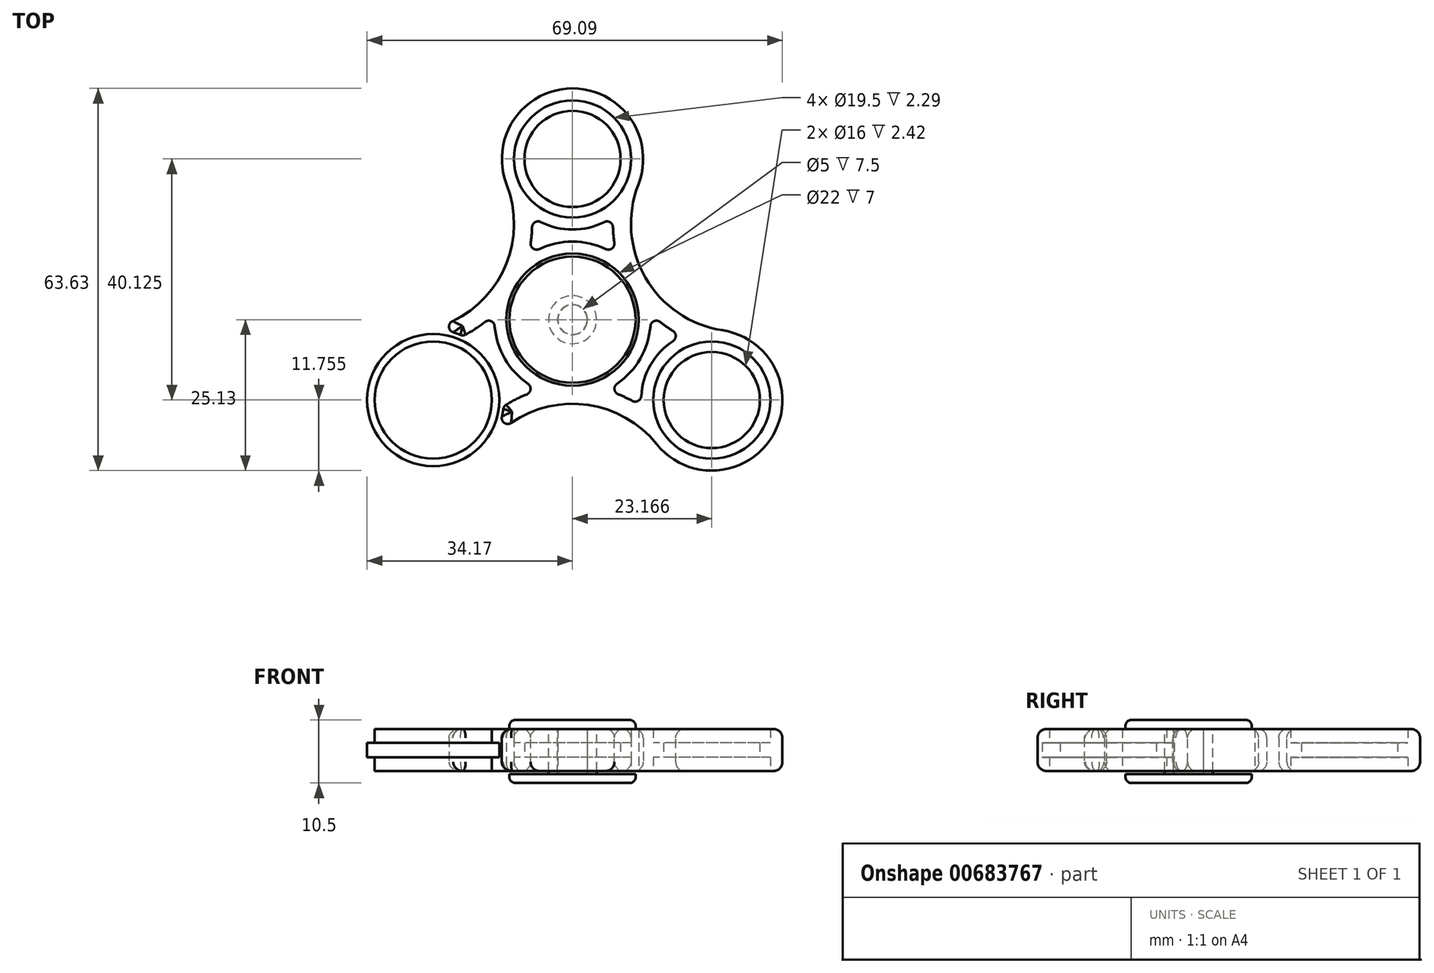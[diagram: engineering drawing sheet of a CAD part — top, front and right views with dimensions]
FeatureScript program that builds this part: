
annotation { "Feature Type Name" : "Feature", "Feature Type Description" : "" }
export const myFeature = defineFeature(function(context is Context, id is Id, definition is map)
    precondition{}
    {
        {
            assignVariable(context, id + "F0", {"name" : "bearing_thickness", "anyValue" : 7});
        }
        {
            assignVariable(context, id + "F1", {"name" : "coin_thickness", "anyValue" : 1.79});
        }
        {
            var Q0;
            Q0=qCreatedBy(makeId("Top.planeOp"),FACE);
            var sketch = newSketch(context, id + "F2", { "sketchPlane" : qUnion([Q0])});
            skCircle(sketch, "E0", {"center": v(0, 0) * mm, "radius": 11 * mm});
            skCircle(sketch, "E1", {"center": v(0, 0) * mm, "radius": 13 * mm});
            skCircle(sketch, "E2", {"center": v(0, 26.75) * mm, "radius": 9.75 * mm});
            skCircle(sketch, "E3", {"center": v(0, 26.75) * mm, "radius": 11.75 * mm});
            skLineSegment(sketch, "E4", {"start": v(0, 0) * mm, "end": v(23.17, -13.37) * mm, "construction": true});
            skLineSegment(sketch, "E5", {"start": v(0, 0) * mm, "end": v(0, 26.75) * mm, "construction": true});
            skCircle(sketch, "E6", {"center": v(23.17, -13.38) * mm, "radius": 9.75 * mm});
            skCircle(sketch, "E7", {"center": v(23.17, -13.38) * mm, "radius": 11.75 * mm});
            skCircle(sketch, "E8.MirrorC", {"center": v(-23.17, -13.38) * mm, "radius": 11.75 * mm});
            skCircle(sketch, "E9.MirrorC", {"center": v(-23.17, -13.38) * mm, "radius": 9.75 * mm});
            skLineSegment(sketch, "E10", {"start": v(-23.17, -13.38) * mm, "end": v(0, 26.75) * mm, "construction": true});
            skLineSegment(sketch, "E11", {"start": v(0, 26.75) * mm, "end": v(23.17, -13.38) * mm, "construction": true});
            skLineSegment(sketch, "E12", {"start": v(-23.17, -13.38) * mm, "end": v(23.17, -13.38) * mm, "construction": true});
            skLineSegment(sketch, "E13", {"start": v(6.18, 52.15) * mm, "end": v(-41.18, -29.88) * mm, "construction": true});
            skArc(sketch, "E14", {"start": v(-24.94, -1.76) * mm, "mid": v(-12.12, 7) * mm, "end": v(-10.95, 22.48) * mm});
            skArc(sketch, "E15.1.0", {"start": v(14, -20.72) * mm, "mid": v(0, -14) * mm, "end": v(-14, -20.72) * mm});
            skArc(sketch, "E15.2.0", {"start": v(10.95, 22.48) * mm, "mid": v(12.12, 7) * mm, "end": v(24.94, -1.76) * mm});
            skArc(sketch, "E16", {"start": v(-11.46, -14.42) * mm, "mid": v(-8.61, -12.85) * mm, "end": v(-5.56, -11.75) * mm});
            skArc(sketch, "E17", {"start": v(5.56, -11.75) * mm, "mid": v(8.61, -12.85) * mm, "end": v(11.46, -14.42) * mm});
            skArc(sketch, "E18", {"start": v(18.22, -2.72) * mm, "mid": v(15.44, -1.03) * mm, "end": v(12.96, 1.06) * mm});
            skArc(sketch, "E19", {"start": v(7.4, 10.69) * mm, "mid": v(6.83, 13.89) * mm, "end": v(6.75, 17.14) * mm});
            skArc(sketch, "E20", {"start": v(-18.22, -2.72) * mm, "mid": v(-15.44, -1.03) * mm, "end": v(-12.96, 1.06) * mm});
            skArc(sketch, "E21", {"start": v(-6.75, 17.14) * mm, "mid": v(-6.83, 13.89) * mm, "end": v(-7.4, 10.69) * mm});
            skLineSegment(sketch, "E22", {"start": v(-27.65, 15.97) * mm, "end": v(0, 0) * mm, "construction": true});
            skLineSegment(sketch, "E23", {"start": v(0, 0) * mm, "end": v(27.65, 15.97) * mm, "construction": true});
            skLineSegment(sketch, "E24", {"start": v(0, 0) * mm, "end": v(0, -31.93) * mm, "construction": true});
            skSolve(sketch);
        }
        {
            var Q0;
            Q0=makeQuery(id+"F2.imprint","IMPRINT",FACE,{"disambiguationData":[TD([[makeQuery(id+"F2.imprint","IMPRINT",EDGE,{"derivedFrom":sQuery(id+"F2.wireOp",EDGE,"E2")}),-1.0]])]});
            var Q1;
            {var subQ0=sQuery(id+"F2.wireOp",EDGE,"E14");Q1=makeQuery(id+"F2.imprint","IMPRINT",FACE,{"disambiguationData":[TD([[makeQuery(id+"F2.imprint","IMPRINT",EDGE,{"derivedFrom":subQ0}),-1.0]])]});}
            var Q2;
            {var subQ0=sQuery(id+"F2.wireOp",EDGE,"E15.2.0");Q2=makeQuery(id+"F2.imprint","IMPRINT",FACE,{"disambiguationData":[TD([[makeQuery(id+"F2.imprint","IMPRINT",EDGE,{"derivedFrom":subQ0}),-1.0]])]});}
            var Q3;
            Q3=makeQuery(id+"F2.imprint","IMPRINT",FACE,{"disambiguationData":[TD([[makeQuery(id+"F2.imprint","IMPRINT",EDGE,{"derivedFrom":sQuery(id+"F2.wireOp",EDGE,"E6")}),-1.0]])]});
            var Q4;
            {var subQ0=sQuery(id+"F2.wireOp",EDGE,"E15.1.0");Q4=makeQuery(id+"F2.imprint","IMPRINT",FACE,{"disambiguationData":[TD([[makeQuery(id+"F2.imprint","IMPRINT",EDGE,{"derivedFrom":subQ0}),-1.0]])]});}
            var Q5;
            Q5=makeQuery(id+"F2.imprint","IMPRINT",FACE,{"disambiguationData":[TD([[makeQuery(id+"F2.imprint","IMPRINT",EDGE,{"derivedFrom":sQuery(id+"F2.wireOp",EDGE,"E9.MirrorC")}),1.0]])]});
            var Q6;
            Q6=makeQuery(id+"F2.imprint","IMPRINT",FACE,{"disambiguationData":[TD([[makeQuery(id+"F2.imprint","IMPRINT",EDGE,{"derivedFrom":sQuery(id+"F2.wireOp",EDGE,"E0")}),-1.0]])]});
            extrude(context, id + "F3", {"entities" : qUnion([Q0, Q1, Q2, Q3, Q4, Q5, Q6]), "depth" : (getVariable(context, 'bearing_thickness')) * mm, "offsetDistance" : 25 * mm});
        }
        {
            var Q0;
            Q0=makeQuery(id+"F3.opExtrude","SWEPT_EDGE",EDGE,{"disambiguationData":[OSD([sQuery(id+"F2.wireOp",EDGE,"E3"),sQuery(id+"F2.wireOp",EDGE,"8bf2e3d8-5615-4718-9600-4cf8535fb07a.trimOffspring")])]});
            var Q1;
            Q1=makeQuery(id+"F3.opExtrude","SWEPT_EDGE",EDGE,{"disambiguationData":[OSD([sQuery(id+"F2.wireOp",EDGE,"E3"),sQuery(id+"F2.wireOp",EDGE,"a5741abb-2599-4cf7-b8e6-df64fac0e9c5.trimOffspring")])]});
            var Q2;
            Q2=makeQuery(id+"F3.opExtrude","SWEPT_EDGE",EDGE,{"disambiguationData":[OSD([sQuery(id+"F2.wireOp",EDGE,"E1"),sQuery(id+"F2.wireOp",EDGE,"8bf2e3d8-5615-4718-9600-4cf8535fb07a.trimOffspring")])]});
            var Q3;
            Q3=makeQuery(id+"F3.opExtrude","SWEPT_EDGE",EDGE,{"disambiguationData":[OSD([sQuery(id+"F2.wireOp",EDGE,"E1"),sQuery(id+"F2.wireOp",EDGE,"a5741abb-2599-4cf7-b8e6-df64fac0e9c5.trimOffspring")])]});
            var Q4;
            Q4=makeQuery(id+"F3.opExtrude","SWEPT_EDGE",EDGE,{"disambiguationData":[OSD([sQuery(id+"F2.wireOp",EDGE,"E7"),sQuery(id+"F2.wireOp",EDGE,"336d5f12-412a-4e1d-b3b8-37471ca9ab7e.trimOffspring")])]});
            var Q5;
            Q5=makeQuery(id+"F3.opExtrude","SWEPT_EDGE",EDGE,{"disambiguationData":[OSD([sQuery(id+"F2.wireOp",EDGE,"E1"),sQuery(id+"F2.wireOp",EDGE,"336d5f12-412a-4e1d-b3b8-37471ca9ab7e.trimOffspring")])]});
            var Q6;
            Q6=makeQuery(id+"F3.opExtrude","SWEPT_EDGE",EDGE,{"disambiguationData":[OSD([sQuery(id+"F2.wireOp",EDGE,"E1"),sQuery(id+"F2.wireOp",EDGE,"f4dcb5e2-fab5-4d8d-8cc3-e8628036cf0f.trimOffspring")])]});
            var Q7;
            Q7=makeQuery(id+"F3.opExtrude","SWEPT_EDGE",EDGE,{"disambiguationData":[OSD([sQuery(id+"F2.wireOp",EDGE,"E7"),sQuery(id+"F2.wireOp",EDGE,"f4dcb5e2-fab5-4d8d-8cc3-e8628036cf0f.trimOffspring")])]});
            var Q8;
            Q8=makeQuery(id+"F3.opExtrude","SWEPT_EDGE",EDGE,{"disambiguationData":[OSD([sQuery(id+"F2.wireOp",EDGE,"E1"),sQuery(id+"F2.wireOp",EDGE,"8b9473ec-3ca8-44b6-a831-62ebe32cb006.trimOffspring")])]});
            var Q9;
            Q9=makeQuery(id+"F3.opExtrude","SWEPT_EDGE",EDGE,{"disambiguationData":[OSD([sQuery(id+"F2.wireOp",EDGE,"E8.MirrorC"),sQuery(id+"F2.wireOp",EDGE,"8b9473ec-3ca8-44b6-a831-62ebe32cb006.trimOffspring")])]});
            var Q10;
            Q10=makeQuery(id+"F3.opExtrude","SWEPT_EDGE",EDGE,{"disambiguationData":[OSD([sQuery(id+"F2.wireOp",EDGE,"E8.MirrorC"),sQuery(id+"F2.wireOp",EDGE,"a5d12814-47ba-4dec-aad6-e72ed20c2dc8.trimOffspring")])]});
            var Q11;
            Q11=makeQuery(id+"F3.opExtrude","SWEPT_EDGE",EDGE,{"disambiguationData":[OSD([sQuery(id+"F2.wireOp",EDGE,"E1"),sQuery(id+"F2.wireOp",EDGE,"a5d12814-47ba-4dec-aad6-e72ed20c2dc8.trimOffspring")])]});
            fillet(context, id + "F4", {"entities" : qUnion([Q0, Q1, Q2, Q3, Q4, Q5, Q6, Q7, Q8, Q9, Q10, Q11]), "radius" : 1 * mm, "tangentPropagation" : true, "allowEdgeOverflow" : false});
        }
        {
            var Q0;
            Q0=makeQuery(id+"F3.opExtrude","CAP_EDGE",EDGE,{"disambiguationData":[OSD([sQuery(id+"F2.wireOp",EDGE,"E14")])],"isStart":false});
            var Q1;
            {var subQ0=sQuery(id+"F2.wireOp",EDGE,"E3");Q1=makeQuery(id+"F3.opExtrude","CAP_EDGE",EDGE,{"disambiguationData":[OSD([subQ0]),TDD([makeQuery(id+"F2.imprint","IMPRINT",EDGE,{"disambiguationData":[TD([[makeQuery(id+"F2.imprint","INTERSECT",VERTEX,{"derivedFrom":[subQ0,sQuery(id+"F2.wireOp",EDGE,"a5741abb-2599-4cf7-b8e6-df64fac0e9c5.trimOffspring")]}),1.0]])],"derivedFrom":subQ0})])],"isStart":false});}
            var Q2;
            {var subQ0=sQuery(id+"F2.wireOp",EDGE,"E1");Q2=makeQuery(id+"F3.opExtrude","CAP_EDGE",EDGE,{"disambiguationData":[OSD([subQ0]),TDD([makeQuery(id+"F2.imprint","IMPRINT",EDGE,{"disambiguationData":[TD([[makeQuery(id+"F2.imprint","INTERSECT",VERTEX,{"derivedFrom":[subQ0,sQuery(id+"F2.wireOp",EDGE,"f4dcb5e2-fab5-4d8d-8cc3-e8628036cf0f.trimOffspring")]}),-1.0]])],"derivedFrom":subQ0})])],"isStart":false});}
            var Q3;
            {var subQ0=sQuery(id+"F2.wireOp",EDGE,"E8.MirrorC");Q3=makeQuery(id+"F3.opExtrude","CAP_EDGE",EDGE,{"disambiguationData":[OSD([subQ0]),TDD([makeQuery(id+"F2.imprint","IMPRINT",EDGE,{"disambiguationData":[TD([[makeQuery(id+"F2.imprint","INTERSECT",VERTEX,{"derivedFrom":[subQ0,sQuery(id+"F2.wireOp",EDGE,"a5d12814-47ba-4dec-aad6-e72ed20c2dc8.trimOffspring")]}),1.0]])],"derivedFrom":subQ0})])],"isStart":false});}
            var Q4;
            Q4=makeQuery(id+"F3.opExtrude","CAP_EDGE",EDGE,{"disambiguationData":[OSD([sQuery(id+"F2.wireOp",EDGE,"E15.1.0")])],"isStart":true});
            var Q5;
            {var subQ0=sQuery(id+"F2.wireOp",EDGE,"E8.MirrorC");Q5=makeQuery(id+"F3.opExtrude","CAP_EDGE",EDGE,{"disambiguationData":[OSD([subQ0]),TDD([makeQuery(id+"F2.imprint","IMPRINT",EDGE,{"disambiguationData":[TD([[makeQuery(id+"F2.imprint","INTERSECT",VERTEX,{"derivedFrom":[subQ0,sQuery(id+"F2.wireOp",EDGE,"a5d12814-47ba-4dec-aad6-e72ed20c2dc8.trimOffspring")]}),1.0]])],"derivedFrom":subQ0})])],"isStart":true});}
            var Q6;
            {var subQ0=sQuery(id+"F2.wireOp",EDGE,"E7");Q6=makeQuery(id+"F3.opExtrude","CAP_EDGE",EDGE,{"disambiguationData":[OSD([subQ0]),TDD([makeQuery(id+"F2.imprint","IMPRINT",EDGE,{"disambiguationData":[TD([[makeQuery(id+"F2.imprint","INTERSECT",VERTEX,{"derivedFrom":[subQ0,sQuery(id+"F2.wireOp",EDGE,"f4dcb5e2-fab5-4d8d-8cc3-e8628036cf0f.trimOffspring")]}),1.0]])],"derivedFrom":subQ0})])],"isStart":true});}
            var Q7;
            {var subQ0=sQuery(id+"F2.wireOp",EDGE,"E1");Q7=makeQuery(id+"F3.opExtrude","CAP_EDGE",EDGE,{"disambiguationData":[OSD([subQ0]),TDD([makeQuery(id+"F2.imprint","IMPRINT",EDGE,{"disambiguationData":[TD([[makeQuery(id+"F2.imprint","INTERSECT",VERTEX,{"derivedFrom":[subQ0,sQuery(id+"F2.wireOp",EDGE,"a5741abb-2599-4cf7-b8e6-df64fac0e9c5.trimOffspring")]}),-1.0]])],"derivedFrom":subQ0})])],"isStart":true});}
            fillet(context, id + "F5", {"entities" : qUnion([Q0, Q1, Q2, Q3, Q4, Q5, Q6, Q7]), "radius" : 1.5 * mm, "tangentPropagation" : true, "allowEdgeOverflow" : false});
        }
        {
            var Q0;
            Q0=qCreatedBy(makeId("Top.planeOp"),FACE);
            cPlane(context, id + "F6", {"entities" : qUnion([Q0]), "cplaneType" : CPlaneType.OFFSET, "offset" : (getVariable(context, 'bearing_thickness') / 2) * mm, "width" : 150 * mm, "height" : 150 * mm});
        }
        {
            var Q0;
            Q0=qCreatedBy(id+"F6.planeOp",FACE);
            var sketch = newSketch(context, id + "F7", { "sketchPlane" : qUnion([Q0])});
            skCircle(sketch, "E25", {"center": v(0, 26.75) * mm, "radius": 11 * mm});
            skCircle(sketch, "E26", {"center": v(0, 26.75) * mm, "radius": 8 * mm});
            skCircle(sketch, "E27.1.0", {"center": v(-23.17, -13.37) * mm, "radius": 11 * mm});
            skCircle(sketch, "E27.1.1", {"center": v(-23.17, -13.37) * mm, "radius": 8 * mm});
            skCircle(sketch, "E27.2.0", {"center": v(23.17, -13.37) * mm, "radius": 11 * mm});
            skCircle(sketch, "E27.2.1", {"center": v(23.17, -13.37) * mm, "radius": 8 * mm});
            skPoint(sketch, "E27.center", {"position": v(0, 0) * mm});
            skSolve(sketch);
        }
        {
            var Q0;
            Q0=makeQuery(id+"F7.imprint","IMPRINT",FACE,{"disambiguationData":[TD([[makeQuery(id+"F7.imprint","IMPRINT",EDGE,{"derivedFrom":sQuery(id+"F7.wireOp",EDGE,"E25")}),1.0]])]});
            var Q1;
            Q1=makeQuery(id+"F7.imprint","IMPRINT",FACE,{"disambiguationData":[TD([[makeQuery(id+"F7.imprint","IMPRINT",EDGE,{"derivedFrom":sQuery(id+"F7.wireOp",EDGE,"E27.1.0")}),1.0]])]});
            var Q2;
            Q2=makeQuery(id+"F7.imprint","IMPRINT",FACE,{"disambiguationData":[TD([[makeQuery(id+"F7.imprint","IMPRINT",EDGE,{"derivedFrom":sQuery(id+"F7.wireOp",EDGE,"E27.2.0")}),1.0]])]});
            extrude(context, id + "F8", {"entities" : qUnion([Q0, Q1, Q2]), "operationType" : NewBodyOperationType.ADD, "endBound" : BoundingType.SYMMETRIC, "depth" : (getVariable(context, 'bearing_thickness') - 2 * getVariable(context, 'coin_thickness') - 1) * mm, "offsetDistance" : 25 * mm});
        }
        {
            var Q0;
            Q0=makeQuery(id+"F5.opFillet","SPLIT",FACE,{"disambiguationData":[OD(3.0)],"derivedFrom":makeQuery(id+"F3.opExtrude","CAP_FACE",FACE,{"disambiguationData":[OSD([sQuery(id+"F2.wireOp",EDGE,"E0"),sQuery(id+"F2.wireOp",EDGE,"E1"),sQuery(id+"F2.wireOp",EDGE,"E2"),sQuery(id+"F2.wireOp",EDGE,"E3"),sQuery(id+"F2.wireOp",EDGE,"E6"),sQuery(id+"F2.wireOp",EDGE,"E7"),sQuery(id+"F2.wireOp",EDGE,"E8.MirrorC"),sQuery(id+"F2.wireOp",EDGE,"E9.MirrorC"),sQuery(id+"F2.wireOp",EDGE,"E14"),sQuery(id+"F2.wireOp",EDGE,"E15.1.0"),sQuery(id+"F2.wireOp",EDGE,"E15.2.0"),sQuery(id+"F2.wireOp",EDGE,"E16"),sQuery(id+"F2.wireOp",EDGE,"E17"),sQuery(id+"F2.wireOp",EDGE,"E18"),sQuery(id+"F2.wireOp",EDGE,"E19"),sQuery(id+"F2.wireOp",EDGE,"E20"),sQuery(id+"F2.wireOp",EDGE,"E21")])],"isStart":false})});
            var sketch = newSketch(context, id + "F9", { "sketchPlane" : qUnion([Q0])});
            skCircle(sketch, "E28", {"center": v(0, 0) * mm, "radius": 10.5 * mm});
            skSolve(sketch);
        }
        {
            var Q0;
            Q0=makeQuery(id+"F9.imprint","IMPRINT",FACE,{"disambiguationData":[TD([[makeQuery(id+"F9.imprint","IMPRINT",EDGE,{"derivedFrom":sQuery(id+"F9.wireOp",EDGE,"E28")}),1.0]])]});
            extrude(context, id + "F10", {"entities" : qUnion([Q0]), "depth" : 1.5 * mm, "offsetDistance" : 25 * mm});
        }
        {
            var Q0;
            Q0=makeQuery(id+"F10.opExtrude","CAP_FACE",FACE,{"disambiguationData":[OSD([sQuery(id+"F9.wireOp",EDGE,"E28")])],"isStart":true});
            var sketch = newSketch(context, id + "F11", { "sketchPlane" : qUnion([Q0])});
            skCircle(sketch, "E29", {"center": v(0, 0) * mm, "radius": 4 * mm});
            skCircle(sketch, "E30", {"center": v(0, 0) * mm, "radius": 2.5 * mm});
            skSolve(sketch);
        }
        {
            var Q0;
            Q0=makeQuery(id+"F11.imprint","IMPRINT",FACE,{"disambiguationData":[TD([[makeQuery(id+"F11.imprint","IMPRINT",EDGE,{"derivedFrom":sQuery(id+"F11.wireOp",EDGE,"E29")}),1.0]])]});
            extrude(context, id + "F12", {"entities" : qUnion([Q0]), "operationType" : NewBodyOperationType.ADD, "depth" : (getVariable(context, 'bearing_thickness') + 0.5) * mm, "offsetDistance" : 25 * mm});
        }
        {
            var Q0;
            Q0=makeQuery(id+"F12.opExtrude","CAP_FACE",FACE,{"disambiguationData":[OSD([sQuery(id+"F11.wireOp",EDGE,"E29"),sQuery(id+"F11.wireOp",EDGE,"E30")])],"isStart":false});
            var sketch = newSketch(context, id + "F13", { "sketchPlane" : qUnion([Q0])});
            skCircle(sketch, "E31", {"center": v(0, 0) * mm, "radius": 10.5 * mm});
            skSolve(sketch);
        }
        {
            var Q0;
            Q0=makeQuery(id+"F13.imprint","IMPRINT",FACE,{"disambiguationData":[TD([[makeQuery(id+"F13.imprint","IMPRINT",EDGE,{"derivedFrom":sQuery(id+"F13.wireOp",EDGE,"E31")}),1.0]])]});
            var Q1;
            Q1=makeQuery(id+"F13.imprint","IMPRINT",FACE,{"disambiguationData":[TD([[makeQuery(id+"F13.imprint","IMPRINT",EDGE,{"derivedFrom":makeQuery(id+"F12.opExtrude","CAP_EDGE",EDGE,{"disambiguationData":[OSD([sQuery(id+"F11.wireOp",EDGE,"E29")])],"isStart":false})}),1.0]])]});
            var Q2;
            Q2=makeQuery(id+"F13.imprint","IMPRINT",FACE,{"disambiguationData":[TD([[makeQuery(id+"F13.imprint","IMPRINT",EDGE,{"derivedFrom":makeQuery(id+"F12.opExtrude","CAP_EDGE",EDGE,{"disambiguationData":[OSD([sQuery(id+"F11.wireOp",EDGE,"E30")])],"isStart":false})}),1.0]])]});
            extrude(context, id + "F14", {"entities" : qUnion([Q0, Q1, Q2]), "depth" : 1.5 * mm, "offsetDistance" : 25 * mm});
        }
        {
            var Q0;
            Q0=makeQuery(id+"F10.opExtrude","CAP_EDGE",EDGE,{"disambiguationData":[OSD([sQuery(id+"F9.wireOp",EDGE,"E28")])],"isStart":false});
            var Q1;
            Q1=makeQuery(id+"F14.opExtrude","CAP_EDGE",EDGE,{"disambiguationData":[OSD([sQuery(id+"F13.wireOp",EDGE,"E31")])],"isStart":false});
            fillet(context, id + "F15", {"entities" : qUnion([Q0, Q1]), "radius" : 1 * mm, "tangentPropagation" : true, "allowEdgeOverflow" : false});
        }
        {
            var Q0;
            Q0=makeQuery(id+"F14.opExtrude","CAP_FACE",FACE,{"disambiguationData":[OSD([sQuery(id+"F13.wireOp",EDGE,"E31")])],"isStart":true});
            var sketch = newSketch(context, id + "F16", { "sketchPlane" : qUnion([Q0])});
            skCircle(sketch, "E32", {"center": v(0, 0) * mm, "radius": 2.45 * mm});
            skSolve(sketch);
        }
        {
            var Q0;
            Q0=makeQuery(id+"F16.imprint","IMPRINT",FACE,{"disambiguationData":[TD([[makeQuery(id+"F16.imprint","IMPRINT",EDGE,{"derivedFrom":sQuery(id+"F16.wireOp",EDGE,"E32")}),1.0]])]});
            var Q1;
            Q1=makeQuery(id+"F12.boolean.opBoolean","SPLIT",FACE,{"disambiguationData":[TD([makeQuery(id+"F12.opExtrude","SWEPT_FACE",FACE,{"disambiguationData":[OSD([sQuery(id+"F11.wireOp",EDGE,"E30")])]})])],"derivedFrom":makeQuery(id+"F10.opExtrude","CAP_FACE",FACE,{"disambiguationData":[OSD([sQuery(id+"F9.wireOp",EDGE,"E28")])],"isStart":true})});
            extrude(context, id + "F17", {"entities" : qUnion([Q0]), "operationType" : NewBodyOperationType.ADD, "endBound" : BoundingType.UP_TO_SURFACE, "depth" : 25 * mm, "endBoundEntityFace" : qUnion([Q1]), "offsetDistance" : 25 * mm});
        }
    });
